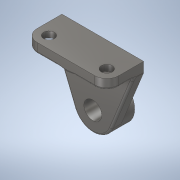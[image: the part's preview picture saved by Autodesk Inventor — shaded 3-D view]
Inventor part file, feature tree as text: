
AUTODESK INVENTOR PART (.ipt)
format: ipt  version: 2020 (Build 240168000, 168)  size: 472,576 bytes
history: native  units: mm
features: extrude x5, sketch x4, fillet x2, plane x1, rib x1
ambient origin geometry x8: Origin, YZ Plane, XZ Plane, XY Plane, X Axis, Y Axis, Z Axis, Center Point
bodies: Solid1 (feature_tree)
feature tree (13):
  extrude  "Extrusion1"  Depth=41.0mm
  sketch  "Sketch2"  dims[d2=18.0mm d3=22.0mm d4=0.0mm]
  extrude  "Extrusion2"  Depth=22.0mm TaperAngle=0.0deg
  extrude  "Extrusion3"  Depth=41.0mm
  plane  "Work Plane1"
  rib  "Rib1"
  sketch  "Sketch6"  dims[d7=10.0mm d8=10.0mm d9=0.0mm d10=27.0mm d11=0.0mm d12=-41.0mm d17=1.0mm d18=10.0mm d19=0.0mm d20=0.0mm d21=1.0mm d22=1.0mm d23=11.0mm d24=22.0mm d25=22.0mm d26=11.0mm d27=12.0mm d28=12.0mm d29=12.0mm d30=12.0mm d31=27.0mm d32=0.0mm d33=4.0mm d34=0.0mm d35=12.0mm d37=2.0mm]
  extrude  "Extrusion4"  Depth=10.0mm TaperAngle=0.0deg
  extrude  "Extrusion5"  Depth=27.0mm TaperAngle=0.0deg
  fillet  "Fillet1"  [1 undecoded]
  fillet  "Fillet3"  Radius=1.0mm
  sketch  "Sketch1"  dims[d0=40.0mm d1=41.0mm]
  sketch  "Sketch5"  dims[d5=82.0mm d6=41.0mm]
note: 1 required parameter value undecoded (feature->parameter linkage not recoverable at this tier; creation-order binding heuristic only, values carry confidence <= 0.55)
